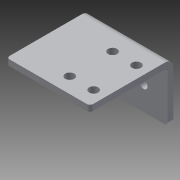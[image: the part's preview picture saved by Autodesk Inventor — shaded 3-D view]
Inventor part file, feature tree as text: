
AUTODESK INVENTOR PART (.ipt)
format: ipt  version: 2014 (Build 180170000, 170)  size: 136,704 bytes
history: native  units: in
note: dims shown in document units (in); Inventor stores cm internally (conversion verified against a paired STEP export)
features: sheet_metal_op x4, sketch x3, other x2, fillet x1, extrude x1
ambient origin geometry x8: Origin, YZ Plane, XZ Plane, XY Plane, X Axis, Y Axis, Z Axis, Center Point
bodies: Solid1 (feature_tree)
feature tree (11):
  sheet_metal_op  "Face1"
  sheet_metal_op  "Flange1"
  fillet  "Fillet1"  Radius=1.75in
  extrude  "Extrusion1"  Depth=0.163in
  sketch  "Sketch1"  dims[d1=1.0in d2=0.163in]
  other  "Plate1"
  sketch  "Sketch2"  dims[d4=0.7874in d6=1.0in d7=0.3937in d9=1.0in]
  other  "Plate2"
  sheet_metal_op  "Bend1"
  sheet_metal_op  "Corner1"
  sketch  "Sketch3"  dims[d11=0.125in d12=0.125in d13=0.0625in d14=0.25in d15=0.125in d16=1.75in d17=90.0deg d18=0.05in d19=0.5in d20=0.125in d21=0.125in d22=0.0625in d23=1.35in d24=0.75in d25=0.125in d27=0.19in d28=0.125in d29=0.2265in d30=1.0in d31=0.0in d34=0.875in d35=0.25in]
